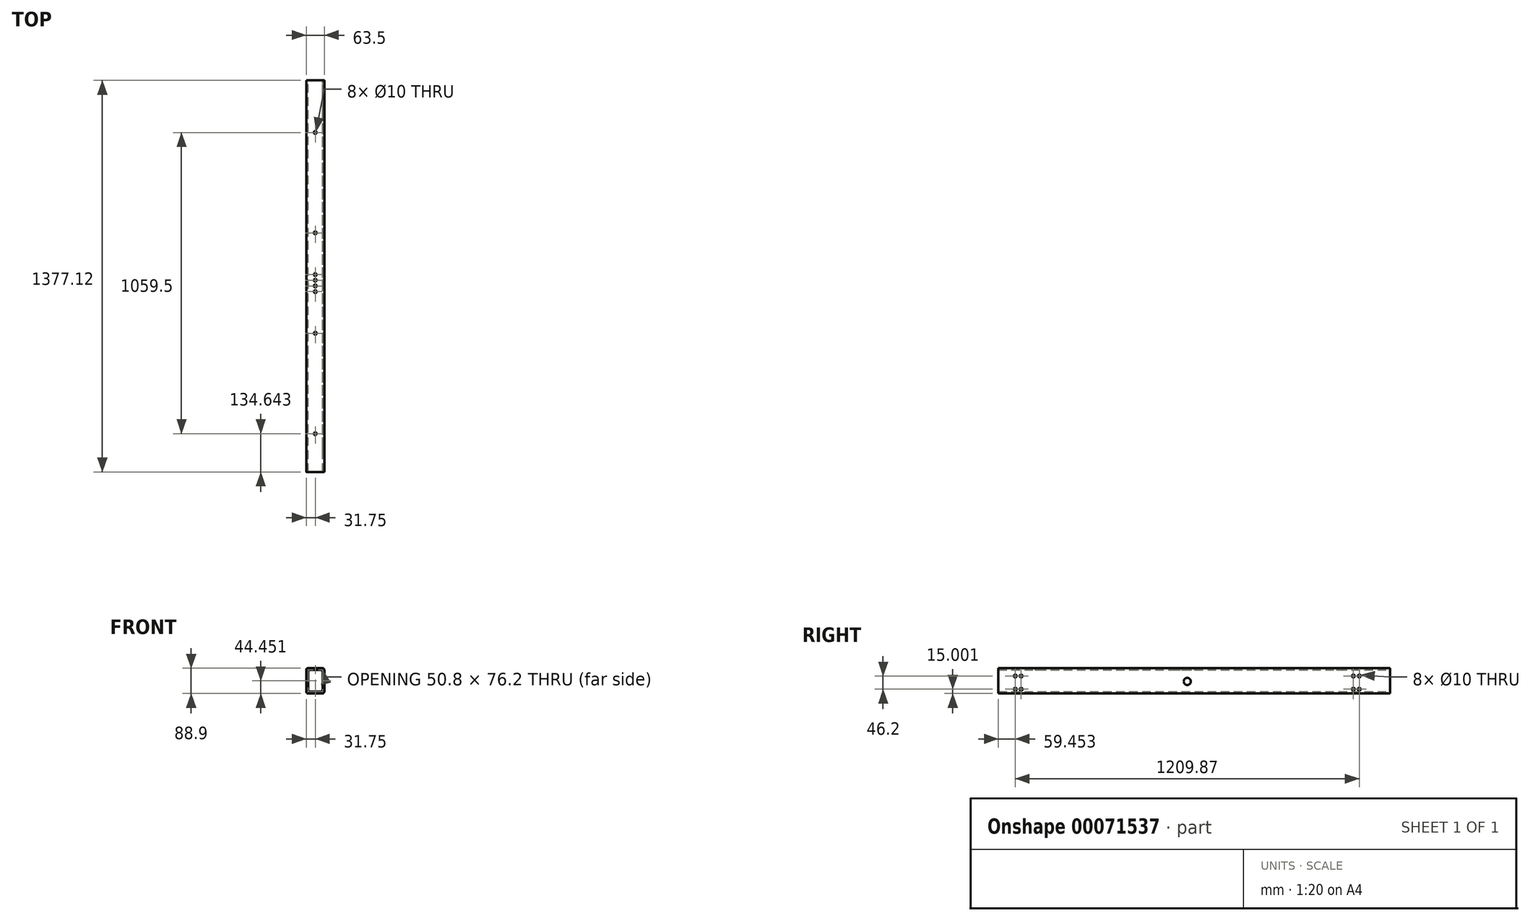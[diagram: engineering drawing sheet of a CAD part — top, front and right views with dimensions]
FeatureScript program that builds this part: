
annotation { "Feature Type Name" : "Feature", "Feature Type Description" : "" }
export const myFeature = defineFeature(function(context is Context, id is Id, definition is map)
    precondition{}
    {
        {
            var Q0;
            Q0=qCreatedBy(makeId("Front.planeOp"),FACE);
            var sketch = newSketch(context, id + "F0", { "sketchPlane" : qUnion([Q0])});
            skLineSegment(sketch, "E0.bottom", {"start": v(-12.7, 49.4) * mm, "end": v(38.1, 49.4) * mm});
            skLineSegment(sketch, "E0.top", {"start": v(-12.7, -39.5) * mm, "end": v(38.1, -39.5) * mm});
            skLineSegment(sketch, "E0.left", {"start": v(-19.05, 43.04) * mm, "end": v(-19.05, -33.16) * mm});
            skLineSegment(sketch, "E0.right", {"start": v(44.45, 43.04) * mm, "end": v(44.45, -33.16) * mm});
            skLineSegment(sketch, "E1.bottom", {"start": v(-6.35, 43.04) * mm, "end": v(31.75, 43.04) * mm});
            skLineSegment(sketch, "E1.top", {"start": v(-6.35, -33.16) * mm, "end": v(31.75, -33.16) * mm});
            skLineSegment(sketch, "E1.left", {"start": v(-12.7, 36.7) * mm, "end": v(-12.7, -26.8) * mm});
            skLineSegment(sketch, "E1.right", {"start": v(38.1, 36.7) * mm, "end": v(38.1, -26.8) * mm});
            skPoint(sketch, "E2.visualSharp", {"position": v(-12.7, 43.04) * mm});
            skArc(sketch, "E2.filletArc", {"start": v(-6.35, 43.04) * mm, "mid": v(-10.84, 41.18) * mm, "end": v(-12.7, 36.7) * mm});
            skPoint(sketch, "E3.visualSharp", {"position": v(38.1, 43.04) * mm});
            skArc(sketch, "E3.filletArc", {"start": v(38.1, 36.7) * mm, "mid": v(36.24, 41.18) * mm, "end": v(31.75, 43.04) * mm});
            skPoint(sketch, "E4.visualSharp", {"position": v(38.1, -33.16) * mm});
            skArc(sketch, "E4.filletArc", {"start": v(31.75, -33.16) * mm, "mid": v(36.24, -31.3) * mm, "end": v(38.1, -26.8) * mm});
            skPoint(sketch, "E5.visualSharp", {"position": v(-12.7, -33.16) * mm});
            skArc(sketch, "E5.filletArc", {"start": v(-12.7, -26.8) * mm, "mid": v(-10.84, -31.3) * mm, "end": v(-6.35, -33.16) * mm});
            skPoint(sketch, "E6.visualSharp", {"position": v(44.45, -39.5) * mm});
            skArc(sketch, "E6.filletArc", {"start": v(38.1, -39.5) * mm, "mid": v(42.6, -37.65) * mm, "end": v(44.45, -33.16) * mm});
            skPoint(sketch, "E7.visualSharp", {"position": v(-19.05, -39.5) * mm});
            skArc(sketch, "E7.filletArc", {"start": v(-19.05, -33.16) * mm, "mid": v(-17.2, -37.65) * mm, "end": v(-12.7, -39.5) * mm});
            skPoint(sketch, "E8.visualSharp", {"position": v(44.45, 49.4) * mm});
            skArc(sketch, "E8.filletArc", {"start": v(44.45, 43.04) * mm, "mid": v(42.6, 47.53) * mm, "end": v(38.1, 49.4) * mm});
            skPoint(sketch, "E9.visualSharp", {"position": v(-19.05, 49.4) * mm});
            skArc(sketch, "E9.filletArc", {"start": v(-12.7, 49.4) * mm, "mid": v(-17.2, 47.53) * mm, "end": v(-19.05, 43.04) * mm});
            skSolve(sketch);
        }
        {
            var Q0;
            Q0=qSketchRegion(id+"F0",true);
            extrude(context, id + "F1", {"entities" : qUnion([Q0]), "depth" : 1377.12 * mm});
        }
        {
            var Q0;
            Q0=makeQuery(id+"F1.opExtrude","SWEPT_FACE",FACE,{"disambiguationData":[OSD([sQuery(id+"F0.wireOp",EDGE,"E0.right")])]});
            var sketch = newSketch(context, id + "F2", { "sketchPlane" : qUnion([Q0])});
            skCircle(sketch, "E10", {"center": v(-1317.67, 21.7) * mm, "radius": 5 * mm});
            skCircle(sketch, "E11.0.1.0", {"center": v(-1317.67, -24.5) * mm, "radius": 5 * mm});
            skCircle(sketch, "E11.1.0.0", {"center": v(-1296.87, 21.7) * mm, "radius": 5 * mm});
            skCircle(sketch, "E11.1.1.0", {"center": v(-1296.87, -24.5) * mm, "radius": 5 * mm});
            skLineSegment(sketch, "E11.direction1", {"start": v(-1317.67, 21.7) * mm, "end": v(-1296.87, 21.7) * mm, "construction": true});
            skLineSegment(sketch, "E11.direction2", {"start": v(-1317.67, 21.7) * mm, "end": v(-1317.67, -24.5) * mm, "construction": true});
            skCircle(sketch, "E12", {"center": v(-128.6, 21.7) * mm, "radius": 5 * mm});
            skCircle(sketch, "E13.0.1.0", {"center": v(-128.6, -24.5) * mm, "radius": 5 * mm});
            skCircle(sketch, "E13.1.0.0", {"center": v(-107.8, 21.7) * mm, "radius": 5 * mm});
            skCircle(sketch, "E13.1.1.0", {"center": v(-107.8, -24.5) * mm, "radius": 5 * mm});
            skLineSegment(sketch, "E13.direction1", {"start": v(-128.6, 21.7) * mm, "end": v(-107.8, 21.7) * mm, "construction": true});
            skLineSegment(sketch, "E13.direction2", {"start": v(-128.6, 21.7) * mm, "end": v(-128.6, -24.5) * mm, "construction": true});
            skSolve(sketch);
        }
        {
            var Q0;
            Q0 = qSketchRegion(id + "F2", true);
            extrude(context, id + "F3", {"entities" : qUnion([Q0]), "operationType" : NewBodyOperationType.REMOVE, "oppositeDirection" : true, "depth" : 25 * mm});
        }
        {
            var Q0;
            Q0=makeQuery(id+"F1.opExtrude","SWEPT_FACE",FACE,{"disambiguationData":[OSD([sQuery(id+"F0.wireOp",EDGE,"E0.bottom")])]});
            var sketch = newSketch(context, id + "F4", { "sketchPlane" : qUnion([Q0])});
            skCircle(sketch, "E14", {"center": v(12.7, -1242.48) * mm, "radius": 5 * mm});
            skCircle(sketch, "E15", {"center": v(12.7, -889.32) * mm, "radius": 5 * mm});
            skCircle(sketch, "E16", {"center": v(12.7, -536.15) * mm, "radius": 5 * mm});
            skCircle(sketch, "E17", {"center": v(12.7, -182.97) * mm, "radius": 5 * mm});
            skCircle(sketch, "E18", {"center": v(12.7, -742.73) * mm, "radius": 5 * mm});
            skCircle(sketch, "E19.0.1.0", {"center": v(12.7, -722.73) * mm, "radius": 5 * mm});
            skCircle(sketch, "E19.0.2.0", {"center": v(12.7, -702.73) * mm, "radius": 5 * mm});
            skCircle(sketch, "E19.0.3.0", {"center": v(12.7, -682.73) * mm, "radius": 5 * mm});
            skLineSegment(sketch, "E19.direction1", {"start": v(12.7, -742.73) * mm, "end": v(38.42, -742.73) * mm, "construction": true});
            skLineSegment(sketch, "E19.direction2", {"start": v(12.7, -742.73) * mm, "end": v(12.7, -722.73) * mm, "construction": true});
            skSolve(sketch);
        }
        {
            var Q0;
            Q0 = qSketchRegion(id + "F4", true);
            extrude(context, id + "F5", {"entities" : qUnion([Q0]), "operationType" : NewBodyOperationType.REMOVE, "oppositeDirection" : true, "depth" : 25 * mm});
        }
        {
            var Q0;
            Q0=makeQuery(id+"F1.opExtrude","SWEPT_FACE",FACE,{"disambiguationData":[OSD([sQuery(id+"F0.wireOp",EDGE,"E0.left")])]});
            var sketch = newSketch(context, id + "F6", { "sketchPlane" : qUnion([Q0])});
            skCircle(sketch, "E20", {"center": v(712.73, 2.7) * mm, "radius": 12.5 * mm});
            skSolve(sketch);
        }
        {
            var Q0;
            Q0 = qSketchRegion(id + "F6", true);
            extrude(context, id + "F7", {"entities" : qUnion([Q0]), "operationType" : NewBodyOperationType.REMOVE, "endBound" : BoundingType.THROUGH_ALL, "oppositeDirection" : true, "depth" : 25 * mm});
        }
    });
